# Revit family: xSanitary_Napkin_Disposal-Bobrick-ClassicSeries-B-3579
name_source: partatom
category: Specialty Equipment
revit_build: Autodesk Revit 2014 (Build: 20130308_1515(x64)
units: mm (PartAtom-declared; Revit-internal decimal feet)

## types (1)
- B-3579
    ADA Compliant = Yes
    Assembly Code = E1010900
    Default Elevation = 60"
    Description = Bobrick ClassicSeries® Surface-Mounted Seat-Cover Dispenser, Sanitary Napkin Disposal, and Toilet Tissue Dispenser
    Height = 30 7/8"
    Installation Type = Wall Mounted
    Length = 4 3/16"
    Manufacturer = Bobrick
    Material = Stainless Steel-Bobrick-Type 304-Satin
    Model = B-3579
    Price = Prices may vary. Please consult Manufacturer Representative for most up-to-date price list.
    Product Documentation Link = http://www.bobrick.com
    Product Page URL = http://www.bobrick.com
    Specification = Surface-mounted toilet-seat-cover dispenser, sanitary napkin disposal, and toilet tissue dispenser shall be type-304 stainless steel; exposed surfaces shall have satin finish. Toilet tissue dispensers shall be ABS plastic. Flange shall be drawn and beveled, onepiece, seamless construction. Unit shall be mounted on side wall of single toilet compartment. Doors shall be one-piece, seamless construction; secured to unit with a full-length stainless steel piano-hinge; and equipped with tumbler locks keyed like other Bobrick washroom accessories. Toilet-seat-cover dispenser shall hold 500 paper covers. Self-closing disposal panel shall be secured to doorwith a spring-loaded, full-length stainless steel piano-hinge has hemmed edges and equipped with an international graphic symbol identifying napkin disposal. Sanitary napkin disposal shall be furnished with a removable, leak-proof, molded polyethylene receptacle with a capacity of 0.8-gal. (3.0-L). Unit shall be equipped with two theft-resistant, heavy-duty ABS toilet tissue spindles that hold standard-core rolls up to 5-1/4'' (135mm) diameter (1800 sheets). Spindles shall be removable from unit only when door is open. Surface-Mounted Seat-Cover Dispenser, Sanitary Napkin Disposal, And Toilet Tissue Dispenser shall be Model B-3579 of Bobrick Washroom Equipment, Inc., Clifton Park, New York; Jackson, Tennessee; Los Angeles, California; Bobrick Washroom Equipment Company, Scarborough, Ontario; Bobrick Washroom Equipment Pty. Ltd., Australia; and Bobrick Washroom Equipment Limited, United Kingdom.
    URL = http://www.bobrick.com
    Warranty Information = 1 Year Limited Warranty
    Width = 17 3/16"

## geometry (parser evidence)
native form markers: Sweep x1
no freeform markers — native parametric forms only
